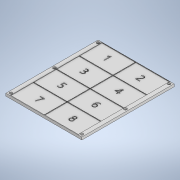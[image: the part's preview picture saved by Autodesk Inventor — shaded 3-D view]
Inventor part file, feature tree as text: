
AUTODESK INVENTOR PART (.ipt)
format: ipt  version: 2020 (Build 240168000, 168)  size: 416,256 bytes
history: native  units: in
note: dims shown in document units (in); Inventor stores cm internally (conversion verified against a paired STEP export)
features: sketch x4, extrude x3, pattern_linear x1, hole x1
ambient origin geometry x8: Origin, YZ Plane, XZ Plane, XY Plane, X Axis, Y Axis, Z Axis, Center Point
bodies: Solid1 (feature_tree)
feature tree (9):
  extrude  "Extrusion1"  Depth=13.854in
  extrude  "Extrusion4"  Depth=0.0787in
  pattern_linear  "Rectangular Pattern1"  Spacing1=0.0787in  [1 undecoded]
  hole  "Hole1"  [1 undecoded]
  extrude  "Extrusion5"  Depth=0.0787in
  sketch  "Sketch1"  dims[d0=11.4173in d1=13.854in]
  sketch  "Sketch2"  dims[d2=0.3937in d3=0.0in d4=0.0787in]
  sketch  "Sketch3"  dims[d5=0.0787in]
  sketch  "Sketch4"  dims[d6=0.0787in d7=0.0787in d8=0.0787in d13=0.0787in d14=0.0787in d17=5.03in d19=0.6195in d20=5.07in d21=3.405in d22=0.0787in d23=0.0787in d24=0.0in d25=0.7874in d27=5.1087in d28=1.5748in d30=3.4437in d31=0.375in d32=0.375in d33=0.375in d34=0.375in d35=0.375in d36=0.375in d37=0.266in d38=0.75in d39=0.438in d40=0.25in d41=0.5635in d42=0.3898in d43=0.0in d44=1.0in d45=0.0in]
note: 2 required parameter values undecoded (feature->parameter linkage not recoverable at this tier; creation-order binding heuristic only, values carry confidence <= 0.55)
